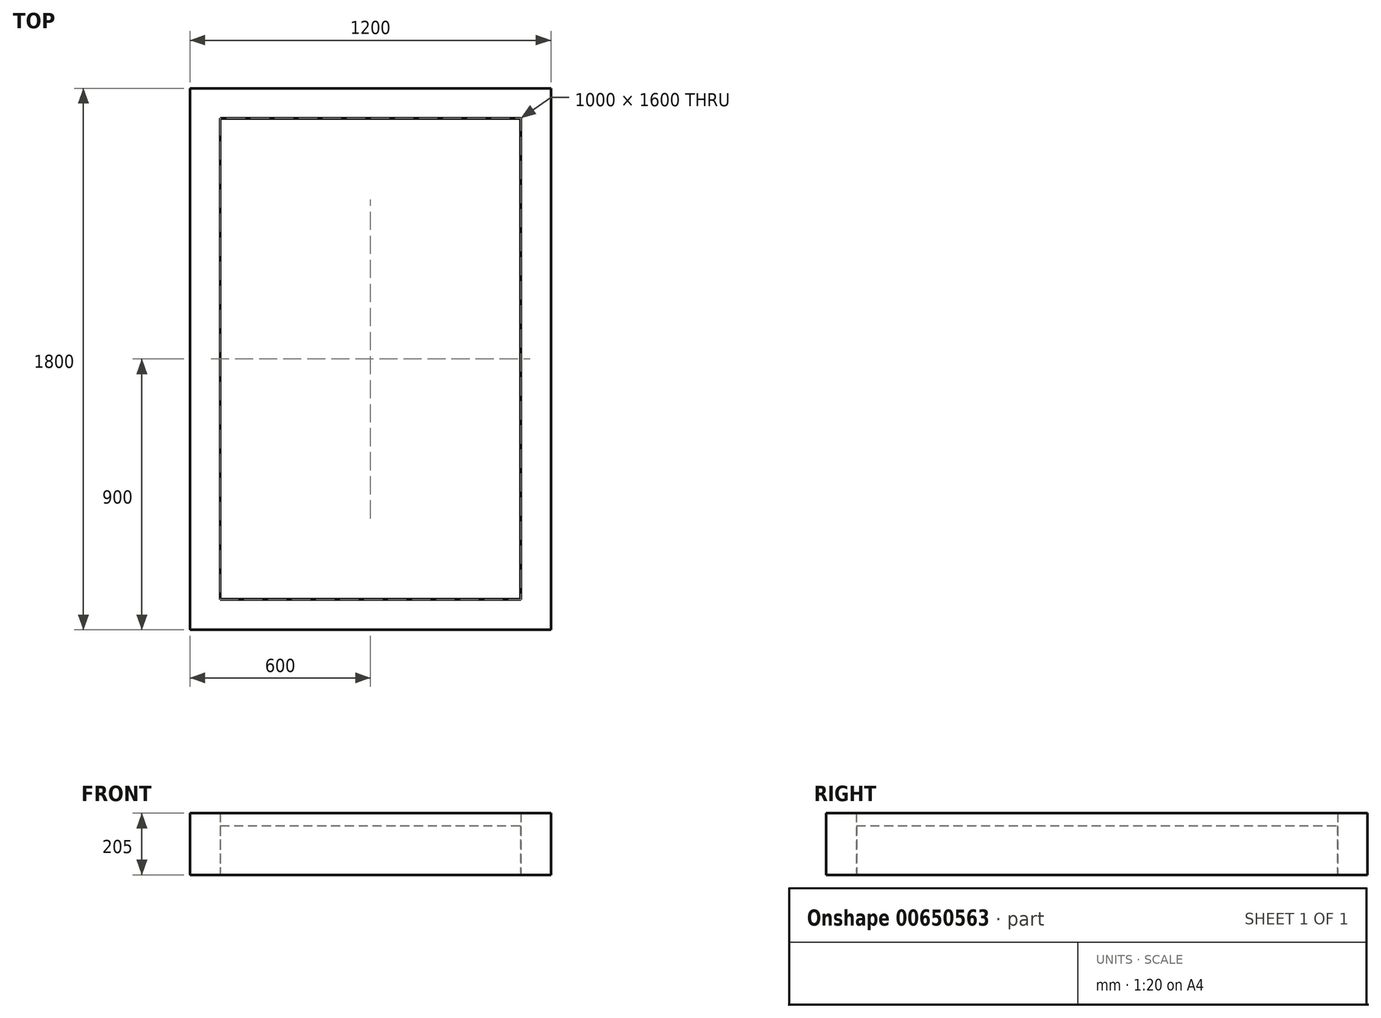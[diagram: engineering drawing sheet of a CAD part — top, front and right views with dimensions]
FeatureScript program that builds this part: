
annotation { "Feature Type Name" : "Feature", "Feature Type Description" : "" }
export const myFeature = defineFeature(function(context is Context, id is Id, definition is map)
    precondition{}
    {
        {
            var Q0;
            Q0=qCreatedBy(makeId("Top.planeOp"),FACE);
            var sketch = newSketch(context, id + "F0", { "sketchPlane" : qUnion([Q0])});
            skLineSegment(sketch, "E0.bottom", {"start": v(0, 0) * mm, "end": v(-1200, 0) * mm});
            skLineSegment(sketch, "E0.top", {"start": v(0, 1800) * mm, "end": v(-1200, 1800) * mm});
            skLineSegment(sketch, "E0.left", {"start": v(0, 0) * mm, "end": v(0, 1800) * mm});
            skLineSegment(sketch, "E0.right", {"start": v(-1200, 0) * mm, "end": v(-1200, 1800) * mm});
            skLineSegment(sketch, "E1.bottom", {"start": v(-100, 100) * mm, "end": v(-1100, 100) * mm});
            skLineSegment(sketch, "E1.top", {"start": v(-100, 1700) * mm, "end": v(-1100, 1700) * mm});
            skLineSegment(sketch, "E1.left", {"start": v(-100, 100) * mm, "end": v(-100, 1700) * mm});
            skLineSegment(sketch, "E1.right", {"start": v(-1100, 100) * mm, "end": v(-1100, 1700) * mm});
            skSolve(sketch);
        }
        {
            var Q0;
            Q0 = qSketchRegion(id + "F0", true);
            extrude(context, id + "F1", {"entities" : qUnion([Q0]), "depth" : 205 * mm, "offsetDistance" : 25 * mm});
        }
        {
            var Q0;
            Q0=qCreatedBy(makeId("Top.planeOp"),FACE);
            var sketch = newSketch(context, id + "F2", { "sketchPlane" : qUnion([Q0])});
            skLineSegment(sketch, "E2.bottom", {"start": v(-1099, 101) * mm, "end": v(-101, 101) * mm});
            skLineSegment(sketch, "E2.top", {"start": v(-1099, 1699) * mm, "end": v(-101, 1699) * mm});
            skLineSegment(sketch, "E2.left", {"start": v(-1099, 101) * mm, "end": v(-1099, 1699) * mm});
            skLineSegment(sketch, "E2.right", {"start": v(-101, 101) * mm, "end": v(-101, 1699) * mm});
            skSolve(sketch);
        }
        {
            var Q0;
            Q0 = qSketchRegion(id + "F2", true);
            extrude(context, id + "F3", {"entities" : qUnion([Q0]), "depth" : 163 * mm, "offsetDistance" : 25 * mm});
        }
    });
